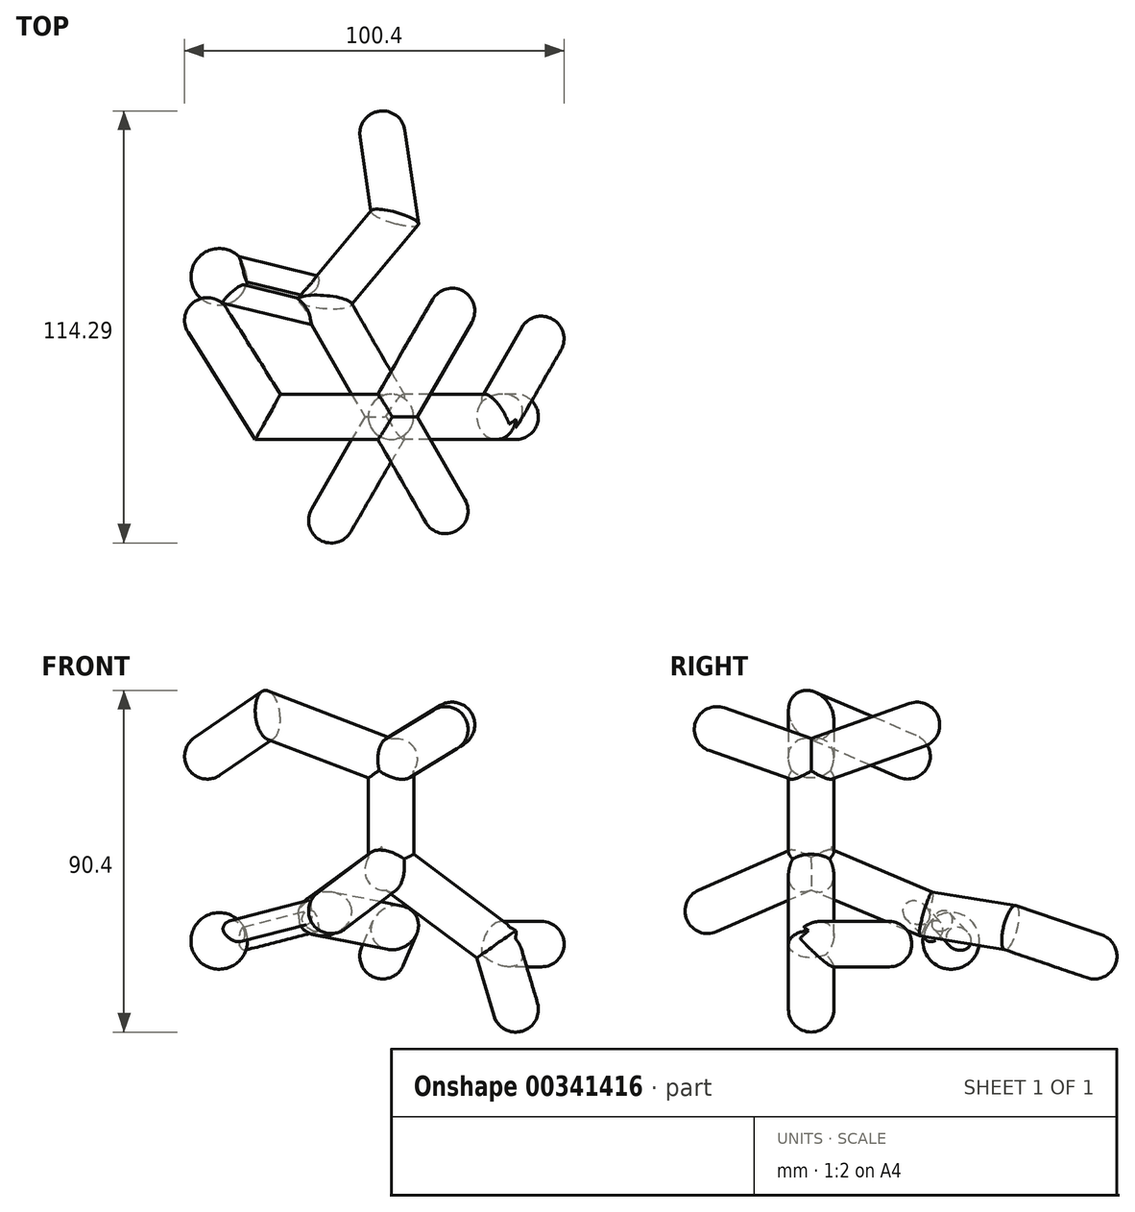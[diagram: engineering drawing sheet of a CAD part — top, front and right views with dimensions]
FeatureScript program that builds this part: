
annotation { "Feature Type Name" : "Feature", "Feature Type Description" : "" }
export const myFeature = defineFeature(function(context is Context, id is Id, definition is map)
    precondition{}
    {
        {
            var Q0;
            Q0=qCreatedBy(makeId("Right.planeOp"),FACE);
            var sketch = newSketch(context, id + "F0", { "sketchPlane" : qUnion([Q0])});
            skLineSegment(sketch, "E0", {"start": v(0, 0) * mm, "end": v(0, 31.61) * mm});
            skLineSegment(sketch, "E1", {"start": v(0, 31.61) * mm, "end": v(0, 87.33) * mm});
            skSolve(sketch);
        }
        {
            var Q0;
            Q0=sQuery(id+"F0.wireOp",EDGE,"E1");
            var Q1;
            Q1=qCreatedBy(makeId("Right.planeOp"),FACE);
            cPlane(context, id + "F1", {"entities" : qUnion([Q0, Q1]), "cplaneType" : CPlaneType.LINE_ANGLE, "offset" : 25 * mm, "angle" : 60 * degree, "width" : 150 * mm, "height" : 150 * mm});
        }
        {
            var Q0;
            Q0=qCreatedBy(makeId("Right.planeOp"),FACE);
            var Q1;
            Q1=sQuery(id+"F0.wireOp",EDGE,"E1");
            cPlane(context, id + "F2", {"entities" : qUnion([Q0, Q1]), "cplaneType" : CPlaneType.LINE_ANGLE, "offset" : 25 * mm, "angle" : 30 * degree, "width" : 150 * mm, "height" : 150 * mm});
        }
        {
            var Q0;
            Q0=qCreatedBy(id+"F2.planeOp",FACE);
            var Q1;
            Q1=sQuery(id+"F0.wireOp",EDGE,"E1");
            cPlane(context, id + "F3", {"entities" : qUnion([Q0, Q1]), "cplaneType" : CPlaneType.LINE_ANGLE, "offset" : 25 * mm, "angle" : 120 * degree, "width" : 150 * mm, "height" : 150 * mm});
        }
        {
            var Q0;
            Q0=qCreatedBy(makeId("Front.planeOp"),FACE);
            var sketch = newSketch(context, id + "F4", { "sketchPlane" : qUnion([Q0])});
            skPoint(sketch, "E2.0", {"position": v(0, 31.61) * mm});
            skLineSegment(sketch, "E3", {"start": v(0, 31.61) * mm, "end": v(27.88, 10.84) * mm});
            skLineSegment(sketch, "E4", {"start": v(27.88, 10.84) * mm, "end": v(34.72, -12.17) * mm});
            skLineSegment(sketch, "E5", {"start": v(0, 31.61) * mm, "end": v(0, 58.91) * mm});
            skSolve(sketch);
        }
        {
            var Q0;
            Q0=qCreatedBy(id+"F2.planeOp",FACE);
            var sketch = newSketch(context, id + "F5", { "sketchPlane" : qUnion([Q0])});
            skPoint(sketch, "E6.0", {"position": v(0, 31.61) * mm});
            skLineSegment(sketch, "E7", {"start": v(0, 31.61) * mm, "end": v(-35.1, 18.85) * mm});
            skSolve(sketch);
        }
        {
            var Q0;
            Q0=sQuery(id+"F5.wireOp",EDGE,"E7");
            var Q1;
            Q1=qCreatedBy(id+"F2.planeOp",FACE);
            cPlane(context, id + "F6", {"entities" : qUnion([Q0, Q1]), "cplaneType" : CPlaneType.LINE_ANGLE, "offset" : 25 * mm, "angle" : 90 * degree, "width" : 150 * mm, "height" : 150 * mm});
        }
        {
            var Q0;
            Q0=qCreatedBy(id+"F6.planeOp",FACE);
            var sketch = newSketch(context, id + "F7", { "sketchPlane" : qUnion([Q0])});
            skLineSegment(sketch, "E8.0", {"start": v(5.15, 9.5) * mm, "end": v(-12.66, -23.34) * mm});
            skLineSegment(sketch, "E9", {"start": v(-12.66, -23.34) * mm, "end": v(6.15, -45.69) * mm});
            skLineSegment(sketch, "E10", {"start": v(6.15, -45.69) * mm, "end": v(2.05, -75.1) * mm});
            skSolve(sketch);
        }
        {
            var Q0;
            Q0=sQuery(id+"F7.wireOp",VERTEX,"E10.end");
            var Q1;
            Q1=sQuery(id+"F7.wireOp",EDGE,"E10");
            cPlane(context, id + "F8", {"entities" : qUnion([Q0, Q1]), "cplaneType" : CPlaneType.LINE_POINT, "offset" : 25 * mm, "width" : 150 * mm, "height" : 150 * mm});
        }
        {
            var Q0;
            Q0=qCreatedBy(id+"F8.planeOp",FACE);
            var sketch = newSketch(context, id + "F9", { "sketchPlane" : qUnion([Q0])});
            skPoint(sketch, "E11.0", {"position": v(-7.1, 31.4) * mm});
            skCircle(sketch, "E12", {"center": v(-7.1, 31.4) * mm, "radius": 6 * mm});
            skSolve(sketch);
        }
        {
            var Q0;
            Q0=qCreatedBy(id+"F3.planeOp",FACE);
            var sketch = newSketch(context, id + "F10", { "sketchPlane" : qUnion([Q0])});
            skPoint(sketch, "E13.0", {"position": v(0, 31.61) * mm});
            skLineSegment(sketch, "E14", {"start": v(0, 31.61) * mm, "end": v(37.22, 17.51) * mm});
            skSolve(sketch);
        }
        {
            var Q0;
            Q0 = qSketchRegion(id + "F9", true);
            var Q1;
            Q1=sQuery(id+"F7.wireOp",EDGE,"E10");
            var Q2;
            Q2=sQuery(id+"F7.wireOp",EDGE,"E9");
            var Q3;
            Q3=sQuery(id+"F7.wireOp",EDGE,"E8.0");
            var Q4;
            Q4=sQuery(id+"F4.wireOp",EDGE,"E5");
            sweep(context, id + "F11", {"profiles" : qUnion([Q0]), "path" : qUnion([Q1, Q2, Q3, Q4])});
        }
        {
            var Q0;
            Q0=sQuery(id+"F4.wireOp",VERTEX,"E4.end");
            var Q1;
            Q1=sQuery(id+"F4.wireOp",EDGE,"E4");
            cPlane(context, id + "F12", {"entities" : qUnion([Q0, Q1]), "cplaneType" : CPlaneType.LINE_POINT, "offset" : 25 * mm, "width" : 150 * mm, "height" : 150 * mm});
        }
        {
            var Q0;
            Q0=qCreatedBy(id+"F12.planeOp",FACE);
            var sketch = newSketch(context, id + "F13", { "sketchPlane" : qUnion([Q0])});
            skPoint(sketch, "E15.0", {"position": v(29.81, 0) * mm});
            skCircle(sketch, "E16", {"center": v(29.81, 0) * mm, "radius": 6 * mm});
            skSolve(sketch);
        }
        {
            var Q0;
            Q0 = qSketchRegion(id + "F13", true);
            var Q1;
            Q1=sQuery(id+"F4.wireOp",EDGE,"E4");
            var Q2;
            Q2=sQuery(id+"F4.wireOp",EDGE,"E3");
            var Q3;
            Q3=sQuery(id+"F10.wireOp",EDGE,"E14");
            sweep(context, id + "F14", {"operationType" : NewBodyOperationType.ADD, "profiles" : qUnion([Q0]), "path" : qUnion([Q1, Q2, Q3])});
        }
        {
            var Q0;
            Q0=qCreatedBy(makeId("Top.planeOp"),FACE);
            var Q1;
            Q1=sQuery(id+"F4.wireOp",VERTEX,"E4.start");
            cPlane(context, id + "F15", {"entities" : qUnion([Q0, Q1]), "cplaneType" : CPlaneType.PLANE_POINT, "offset" : 25 * mm, "width" : 150 * mm, "height" : 150 * mm});
        }
        {
            var Q0;
            Q0=qCreatedBy(id+"F15.planeOp",FACE);
            var sketch = newSketch(context, id + "F16", { "sketchPlane" : qUnion([Q0])});
            skPoint(sketch, "E17.0", {"position": v(27.88, 0) * mm});
            skLineSegment(sketch, "E18", {"start": v(27.88, 0) * mm, "end": v(42.79, 25.82) * mm});
            skSolve(sketch);
        }
        {
            var Q0;
            Q0=sQuery(id+"F16.wireOp",VERTEX,"E18.end");
            var Q1;
            Q1=sQuery(id+"F16.wireOp",EDGE,"E18");
            cPlane(context, id + "F17", {"entities" : qUnion([Q0, Q1]), "cplaneType" : CPlaneType.LINE_POINT, "offset" : 25 * mm, "width" : 150 * mm, "height" : 150 * mm});
        }
        {
            var Q0;
            Q0=qCreatedBy(id+"F17.planeOp",FACE);
            var sketch = newSketch(context, id + "F18", { "sketchPlane" : qUnion([Q0])});
            skPoint(sketch, "E19.0", {"position": v(-24.14, 10.84) * mm});
            skCircle(sketch, "E20", {"center": v(-24.14, 10.84) * mm, "radius": 6 * mm});
            skSolve(sketch);
        }
        {
            var Q0;
            Q0 = qSketchRegion(id + "F18", true);
            var Q1;
            Q1=sQuery(id+"F16.wireOp",EDGE,"E18");
            sweep(context, id + "F19", {"operationType" : NewBodyOperationType.ADD, "profiles" : qUnion([Q0]), "path" : qUnion([Q1])});
        }
        {
            var Q0;
            Q0=qCreatedBy(id+"F3.planeOp",FACE);
            var sketch = newSketch(context, id + "F20", { "sketchPlane" : qUnion([Q0])});
            skPoint(sketch, "E21.0", {"position": v(0, 58.91) * mm});
            skLineSegment(sketch, "E22", {"start": v(0, 58.91) * mm, "end": v(-38.08, 70.63) * mm});
            skSolve(sketch);
        }
        {
            var Q0;
            Q0=qCreatedBy(id+"F2.planeOp",FACE);
            var sketch = newSketch(context, id + "F21", { "sketchPlane" : qUnion([Q0])});
            skPoint(sketch, "E23.0", {"position": v(0, 58.91) * mm});
            skLineSegment(sketch, "E24", {"start": v(0, 58.91) * mm, "end": v(34.5, 69.43) * mm});
            skSolve(sketch);
        }
        {
            var Q0;
            Q0=qCreatedBy(makeId("Front.planeOp"),FACE);
            var sketch = newSketch(context, id + "F22", { "sketchPlane" : qUnion([Q0])});
            skPoint(sketch, "E25.0", {"position": v(0, 58.91) * mm});
            skLineSegment(sketch, "E26", {"start": v(0, 58.91) * mm, "end": v(-32.6, 71.45) * mm});
            skSolve(sketch);
        }
        {
            var Q0;
            Q0=qCreatedBy(id+"F6.planeOp",FACE);
            var Q1;
            Q1=sQuery(id+"F22.wireOp",VERTEX,"E26.end");
            cPlane(context, id + "F23", {"entities" : qUnion([Q0, Q1]), "cplaneType" : CPlaneType.PLANE_POINT, "offset" : 25 * mm, "width" : 150 * mm, "height" : 150 * mm});
        }
        {
            var Q0;
            Q0=qCreatedBy(id+"F23.planeOp",FACE);
            var sketch = newSketch(context, id + "F24", { "sketchPlane" : qUnion([Q0])});
            skPoint(sketch, "E27.0", {"position": v(-20.48, 21.45) * mm});
            skLineSegment(sketch, "E28", {"start": v(-20.48, 21.45) * mm, "end": v(-39.77, -11.35) * mm});
            skSolve(sketch);
        }
        {
            var Q0;
            Q0=sQuery(id+"F21.wireOp",VERTEX,"E24.end");
            var Q1;
            Q1=sQuery(id+"F21.wireOp",EDGE,"E24");
            cPlane(context, id + "F25", {"entities" : qUnion([Q0, Q1]), "cplaneType" : CPlaneType.LINE_POINT, "offset" : 25 * mm, "width" : 150 * mm, "height" : 150 * mm});
        }
        {
            var Q0;
            Q0=qCreatedBy(id+"F25.planeOp",FACE);
            var sketch = newSketch(context, id + "F26", { "sketchPlane" : qUnion([Q0])});
            skPoint(sketch, "E29.0", {"position": v(-9.35, 55.57) * mm});
            skCircle(sketch, "E30", {"center": v(-9.35, 55.57) * mm, "radius": 6 * mm});
            skSolve(sketch);
        }
        {
            var Q0;
            Q0=makeQuery(id+"F26.imprint","IMPRINT",FACE,{"disambiguationData":[TD([[makeQuery(id+"F26.imprint","IMPRINT",EDGE,{"derivedFrom":sQuery(id+"F26.wireOp",EDGE,"E30")}),1.0]])]});
            var Q1;
            Q1=sQuery(id+"F21.wireOp",EDGE,"E24");
            var Q2;
            Q2=sQuery(id+"F20.wireOp",EDGE,"E22");
            sweep(context, id + "F27", {"operationType" : NewBodyOperationType.ADD, "profiles" : qUnion([Q0]), "path" : qUnion([Q1, Q2])});
        }
        {
            var Q0;
            Q0=sQuery(id+"F24.wireOp",EDGE,"E28");
            var Q1;
            Q1=sQuery(id+"F24.wireOp",VERTEX,"E28.end");
            cPlane(context, id + "F28", {"entities" : qUnion([Q0, Q1]), "cplaneType" : CPlaneType.LINE_POINT, "offset" : 25 * mm, "width" : 150 * mm, "height" : 150 * mm});
        }
        {
            var Q0;
            Q0=qCreatedBy(id+"F28.planeOp",FACE);
            var sketch = newSketch(context, id + "F29", { "sketchPlane" : qUnion([Q0])});
            skPoint(sketch, "E31.0", {"position": v(42.3, 65.67) * mm});
            skCircle(sketch, "E32", {"center": v(42.3, 65.67) * mm, "radius": 6 * mm});
            skSolve(sketch);
        }
        {
            var Q0;
            Q0=makeQuery(id+"F29.imprint","IMPRINT",FACE,{"disambiguationData":[TD([[makeQuery(id+"F29.imprint","IMPRINT",EDGE,{"derivedFrom":sQuery(id+"F29.wireOp",EDGE,"E32")}),1.0]])]});
            var Q1;
            Q1=sQuery(id+"F24.wireOp",EDGE,"E28");
            var Q2;
            Q2=sQuery(id+"F22.wireOp",EDGE,"E26");
            sweep(context, id + "F30", {"operationType" : NewBodyOperationType.ADD, "profiles" : qUnion([Q0]), "path" : qUnion([Q1, Q2])});
        }
        {
            var Q0;
            Q0=makeQuery(id+"F14.opSweep","CAP_EDGE",EDGE,{"disambiguationData":[OSD([sQuery(id+"F4.wireOp",VERTEX,"E4.end"),sQuery(id+"F13.wireOp",EDGE,"E16")])],"isStart":true});
            var Q1;
            Q1=makeQuery(id+"F11.opSweep","CAP_EDGE",EDGE,{"disambiguationData":[OSD([sQuery(id+"F7.wireOp",VERTEX,"E10.end"),sQuery(id+"F9.wireOp",EDGE,"E12")])],"isStart":true});
            var Q2;
            Q2=makeQuery(id+"F14.opSweep","CAP_EDGE",EDGE,{"disambiguationData":[OSD([sQuery(id+"F10.wireOp",VERTEX,"E14.end"),sQuery(id+"F13.wireOp",EDGE,"E16")])],"isStart":false});
            var Q3;
            Q3=makeQuery(id+"F19.opSweep","CAP_EDGE",EDGE,{"disambiguationData":[OSD([sQuery(id+"F16.wireOp",VERTEX,"E18.end"),sQuery(id+"F18.wireOp",EDGE,"E20")])],"isStart":true});
            var Q4;
            Q4=makeQuery(id+"F27.opSweep","CAP_EDGE",EDGE,{"disambiguationData":[OSD([sQuery(id+"F20.wireOp",VERTEX,"E22.end"),sQuery(id+"F26.wireOp",EDGE,"E30")])],"isStart":false});
            var Q5;
            Q5=makeQuery(id+"F30.opSweep","CAP_EDGE",EDGE,{"disambiguationData":[OSD([sQuery(id+"F24.wireOp",VERTEX,"E28.end"),sQuery(id+"F29.wireOp",EDGE,"E32")])],"isStart":true});
            var Q6;
            Q6=makeQuery(id+"F27.opSweep","CAP_EDGE",EDGE,{"disambiguationData":[OSD([sQuery(id+"F21.wireOp",VERTEX,"E24.end"),sQuery(id+"F26.wireOp",EDGE,"E30")])],"isStart":true});
            fillet(context, id + "F31", {"entities" : qUnion([Q0, Q1, Q2, Q3, Q4, Q5, Q6]), "radius" : (12 / 2) * mm, "tangentPropagation" : true, "allowEdgeOverflow" : false});
        }
        {
            var Q0;
            Q0=qCreatedBy(id+"F6.planeOp",FACE);
            var sketch = newSketch(context, id + "F32", { "sketchPlane" : qUnion([Q0])});
            skPoint(sketch, "E33.0", {"position": v(-12.66, -23.34) * mm});
            skLineSegment(sketch, "E34", {"start": v(-12.66, -23.34) * mm, "end": v(-41.07, -32.03) * mm});
            skSolve(sketch);
        }
        {
            var Q0;
            Q0=sQuery(id+"F32.wireOp",VERTEX,"E34.end");
            var Q1;
            Q1=sQuery(id+"F32.wireOp",EDGE,"E34");
            cPlane(context, id + "F33", {"entities" : qUnion([Q0, Q1]), "cplaneType" : CPlaneType.LINE_POINT, "offset" : 25 * mm, "width" : 150 * mm, "height" : 150 * mm});
        }
        {
            var Q0;
            Q0=qCreatedBy(id+"F33.planeOp",FACE);
            var sketch = newSketch(context, id + "F34", { "sketchPlane" : qUnion([Q0])});
            skPoint(sketch, "E35.0", {"position": v(-26.76, 22.65) * mm});
            skCircle(sketch, "E36", {"center": v(-23.13, 24.12) * mm, "radius": 3 * mm});
            skCircle(sketch, "E37", {"center": v(-29.96, 21.62) * mm, "radius": 3 * mm});
            skSolve(sketch);
        }
        {
            var Q0;
            Q0=makeQuery(id+"F34.imprint","IMPRINT",FACE,{"disambiguationData":[TD([[makeQuery(id+"F34.imprint","IMPRINT",EDGE,{"derivedFrom":sQuery(id+"F34.wireOp",EDGE,"E36")}),1.0]])]});
            var Q1;
            Q1=makeQuery(id+"F34.imprint","IMPRINT",FACE,{"disambiguationData":[TD([[makeQuery(id+"F34.imprint","IMPRINT",EDGE,{"derivedFrom":sQuery(id+"F34.wireOp",EDGE,"E37")}),1.0]])]});
            var Q2;
            Q2=sQuery(id+"F32.wireOp",EDGE,"E34");
            sweep(context, id + "F35", {"operationType" : NewBodyOperationType.ADD, "profiles" : qUnion([Q0, Q1]), "path" : qUnion([Q2])});
        }
        {
            var Q0;
            Q0=qCreatedBy(id+"F6.planeOp",FACE);
            var sketch = newSketch(context, id + "F36", { "sketchPlane" : qUnion([Q0])});
            skLineSegment(sketch, "E38.0", {"start": v(-43.09, -25.43) * mm, "end": v(-41.33, -31.17) * mm, "construction": true});
            skLineSegment(sketch, "E38.1", {"start": v(-40.96, -32.38) * mm, "end": v(-39.2, -38.12) * mm, "construction": true});
            skArc(sketch, "E39", {"start": v(-48.07, -34.17) * mm, "mid": v(-38.6, -38.93) * mm, "end": v(-33.86, -29.47) * mm});
            skLineSegment(sketch, "E40", {"start": v(-33.86, -29.47) * mm, "end": v(-48.07, -34.17) * mm});
            skSolve(sketch);
        }
        {
            var Q0;
            Q0=makeQuery(id+"F36.imprint","IMPRINT",FACE,{"disambiguationData":[TD([[makeQuery(id+"F36.imprint","IMPRINT",EDGE,{"derivedFrom":sQuery(id+"F36.wireOp",EDGE,"E39")}),1.0]])]});
            var Q1;
            Q1=sQuery(id+"F36.wireOp",EDGE,"E40");
            revolve(context, id + "F37", {"operationType" : NewBodyOperationType.ADD, "entities" : qUnion([Q0]), "axis" : qUnion([Q1]), "revolveType" : RevolveType.FULL});
        }
    });
